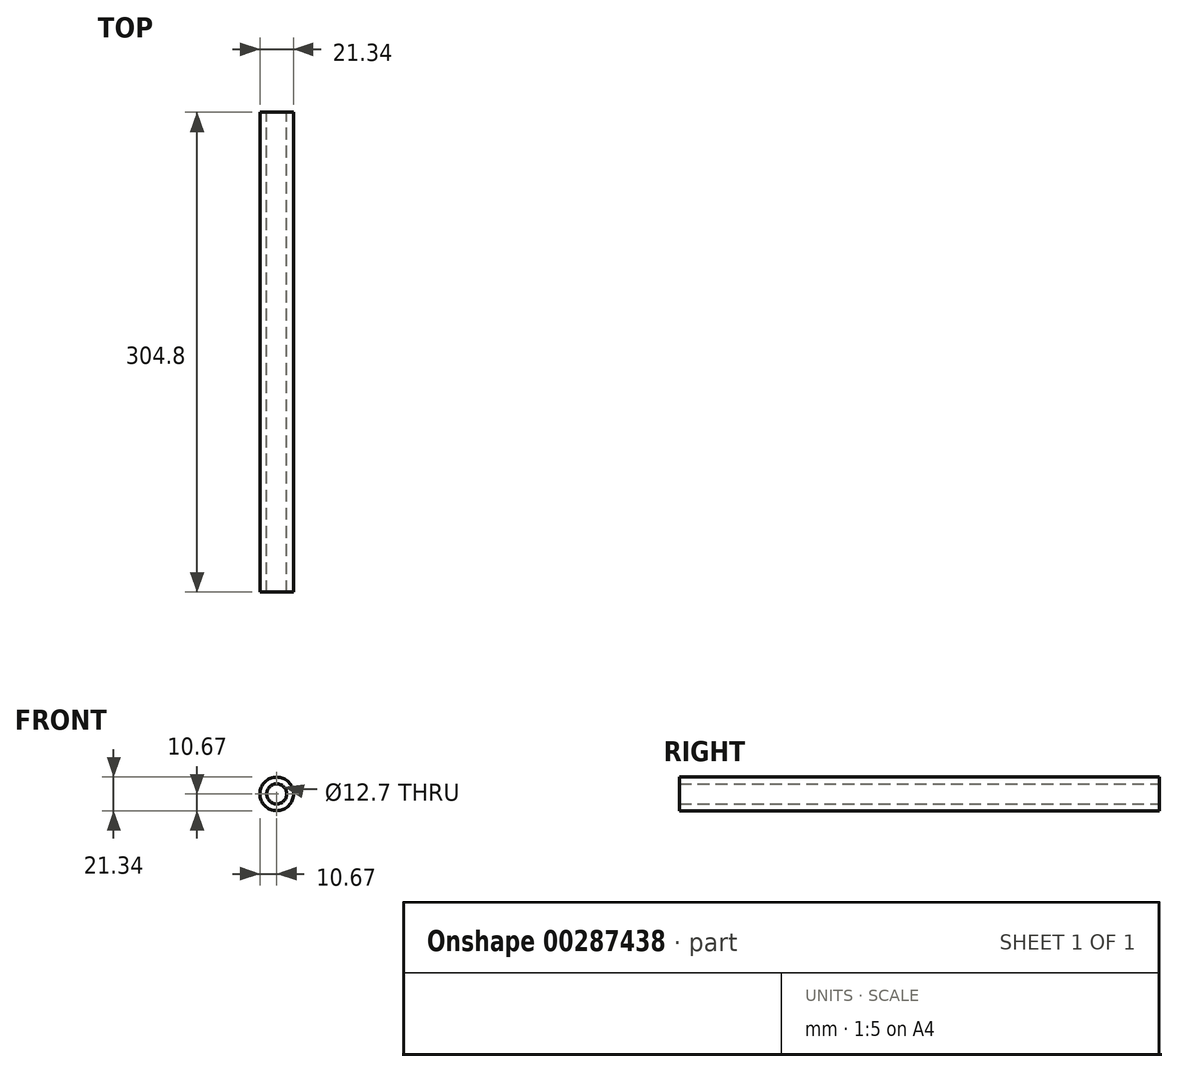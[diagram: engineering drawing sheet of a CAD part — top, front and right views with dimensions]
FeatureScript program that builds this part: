
annotation { "Feature Type Name" : "Feature", "Feature Type Description" : "" }
export const myFeature = defineFeature(function(context is Context, id is Id, definition is map)
    precondition{}
    {
        {
            var Q0;
            Q0=qCreatedBy(makeId("Front.planeOp"),FACE);
            var sketch = newSketch(context, id + "F0", { "sketchPlane" : qUnion([Q0])});
            skCircle(sketch, "E0", {"center": v(0, 0) * mm, "radius": 10.67 * mm});
            skCircle(sketch, "E1", {"center": v(0, 0) * mm, "radius": 6.35 * mm});
            skSolve(sketch);
        }
        {
            var Q0;
            Q0 = qSketchRegion(id + "F0", true);
            extrude(context, id + "F1", {"entities" : qUnion([Q0]), "depth" : 304.8 * mm});
        }
    });
